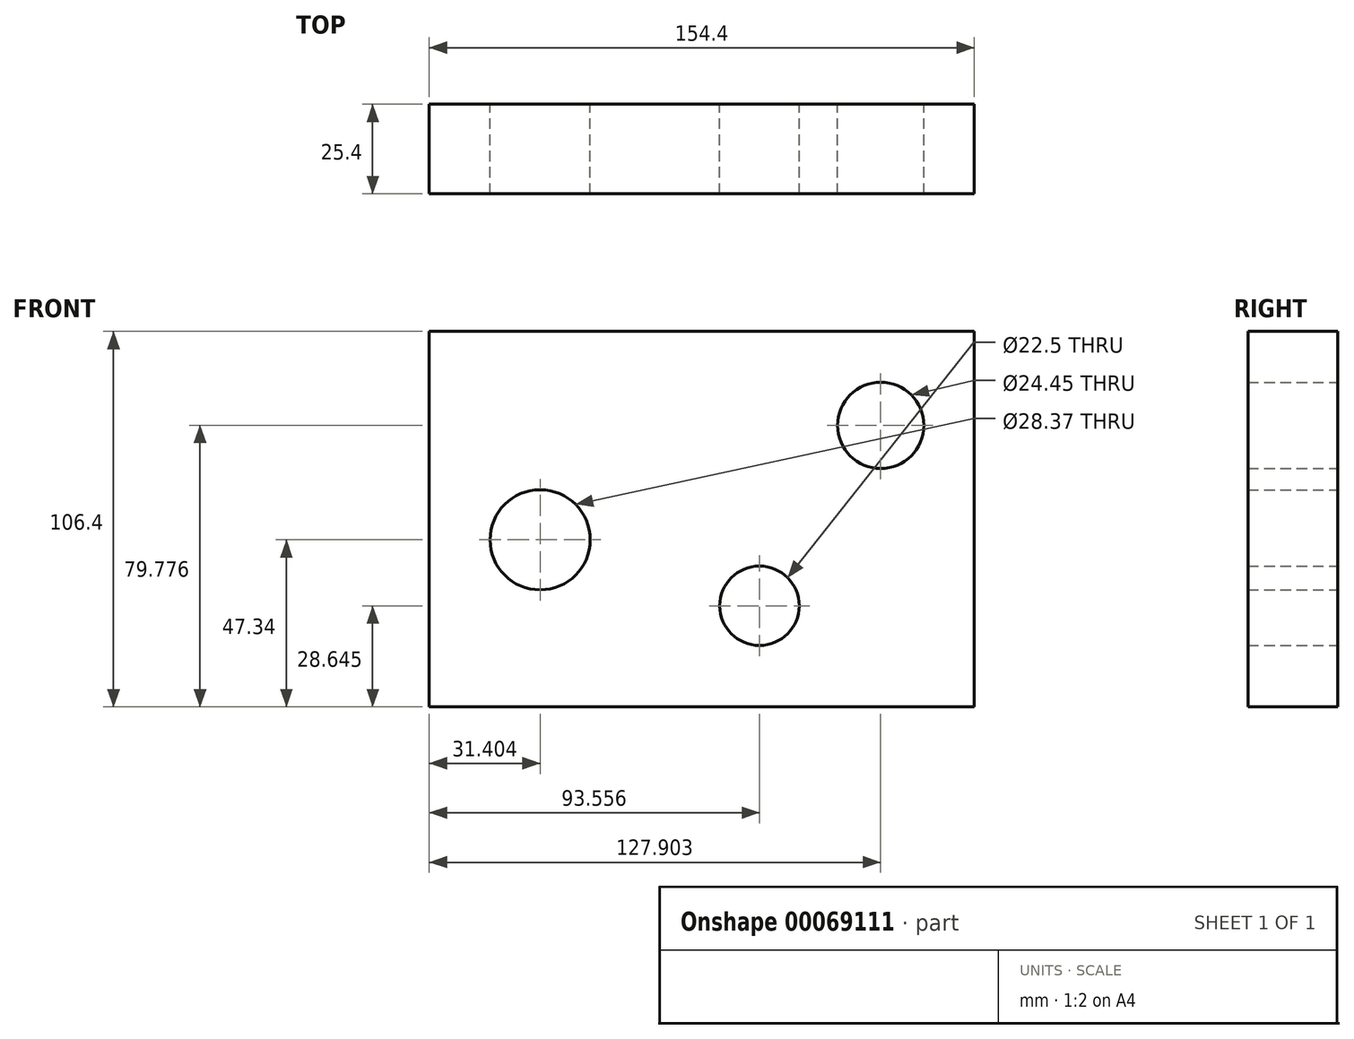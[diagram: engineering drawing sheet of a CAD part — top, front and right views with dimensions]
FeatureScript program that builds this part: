
annotation { "Feature Type Name" : "Feature", "Feature Type Description" : "" }
export const myFeature = defineFeature(function(context is Context, id is Id, definition is map)
    precondition{}
    {
        {
            var Q0;
            Q0=qCreatedBy(makeId("Front.planeOp"),FACE);
            var sketch = newSketch(context, id + "F0", { "sketchPlane" : qUnion([Q0])});
            skLineSegment(sketch, "E0.rect.bottom", {"start": v(77.2, 53.2) * mm, "end": v(-77.2, 53.2) * mm});
            skLineSegment(sketch, "E0.rect.top", {"start": v(77.2, -53.2) * mm, "end": v(-77.2, -53.2) * mm});
            skLineSegment(sketch, "E0.rect.left", {"start": v(77.2, 53.2) * mm, "end": v(77.2, -53.2) * mm});
            skLineSegment(sketch, "E0.rect.right", {"start": v(-77.2, 53.2) * mm, "end": v(-77.2, -53.2) * mm});
            skPoint(sketch, "E0.rect.middle", {"position": v(0, 0) * mm});
            skCircle(sketch, "E1", {"center": v(50.7, 26.58) * mm, "radius": 12.22 * mm});
            skCircle(sketch, "E2", {"center": v(16.36, -24.56) * mm, "radius": 11.25 * mm});
            skCircle(sketch, "E3", {"center": v(-45.8, -5.86) * mm, "radius": 14.18 * mm});
            skSolve(sketch);
        }
        {
            var Q0;
            Q0 = qSketchRegion(id + "F0", true);
            extrude(context, id + "F1", {"entities" : qUnion([Q0]), "depth" : 25.4 * mm});
        }
    });
